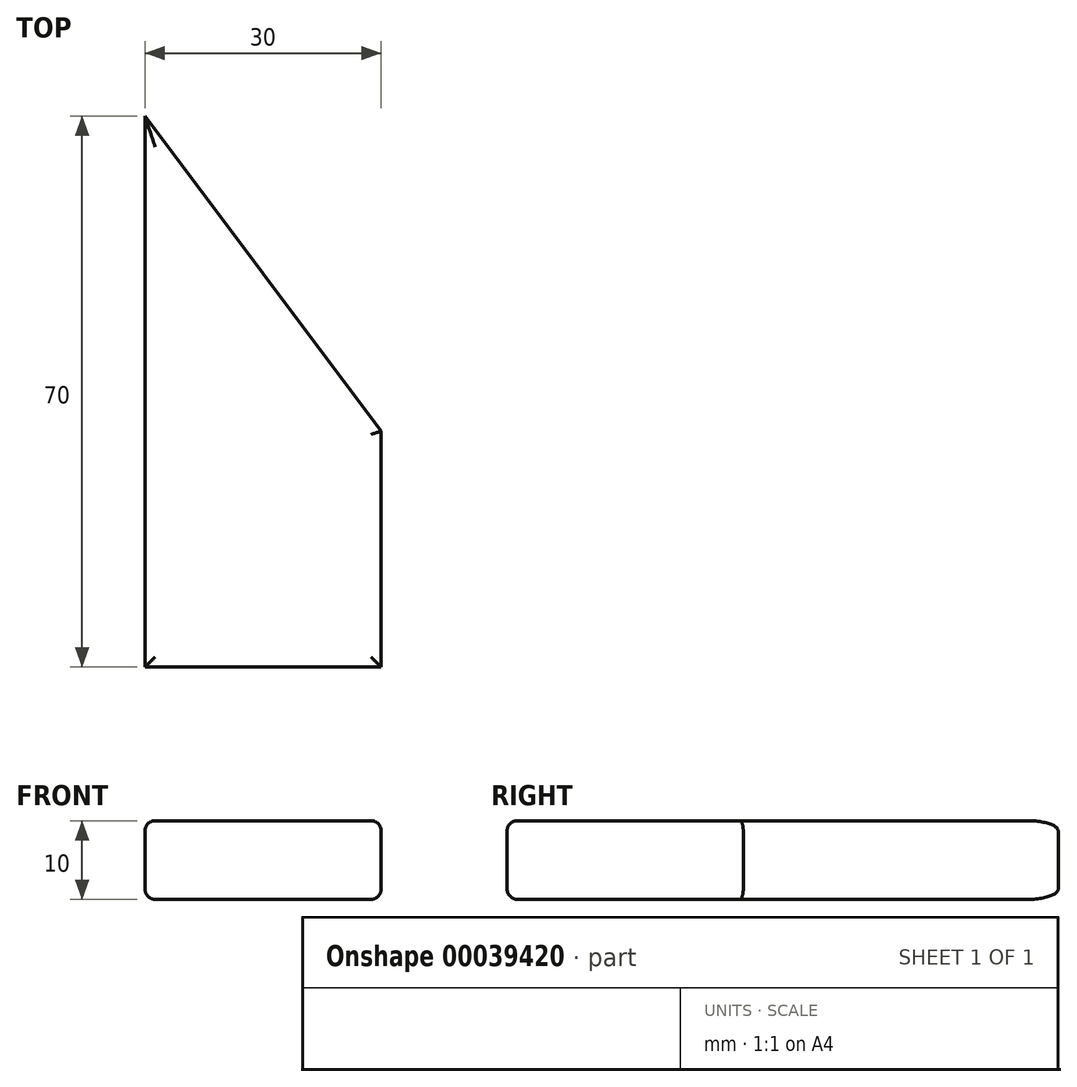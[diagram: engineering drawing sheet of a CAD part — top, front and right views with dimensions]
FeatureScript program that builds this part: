
annotation { "Feature Type Name" : "Feature", "Feature Type Description" : "" }
export const myFeature = defineFeature(function(context is Context, id is Id, definition is map)
    precondition{}
    {
        {
            var Q0;
            Q0=qCreatedBy(makeId("Top.planeOp"),FACE);
            var sketch = newSketch(context, id + "F0", { "sketchPlane" : qUnion([Q0])});
            skLineSegment(sketch, "E0.bottom", {"start": v(-37.15, -6.24) * mm, "end": v(-7.15, -6.24) * mm});
            skLineSegment(sketch, "E0.top", {"start": v(-37.15, -36.24) * mm, "end": v(-7.15, -36.24) * mm});
            skLineSegment(sketch, "E0.left", {"start": v(-37.15, -6.24) * mm, "end": v(-37.15, -36.24) * mm});
            skLineSegment(sketch, "E0.right", {"start": v(-7.15, -6.24) * mm, "end": v(-7.15, -36.24) * mm});
            skLineSegment(sketch, "E1", {"start": v(-37.15, -6.24) * mm, "end": v(-37.15, 33.76) * mm});
            skLineSegment(sketch, "E2", {"start": v(-7.15, -6.24) * mm, "end": v(-37.15, 33.76) * mm});
            skSolve(sketch);
        }
        {
            var Q0;
            Q0=makeQuery(id+"F0.imprint","IMPRINT",FACE,{"disambiguationData":[TD([[makeQuery(id+"F0.imprint","IMPRINT",EDGE,{"derivedFrom":sQuery(id+"F0.wireOp",EDGE,"E0.bottom")}),1.0]])]});
            var Q1;
            Q1=makeQuery(id+"F0.imprint","IMPRINT",FACE,{"disambiguationData":[TD([[makeQuery(id+"F0.imprint","IMPRINT",EDGE,{"derivedFrom":sQuery(id+"F0.wireOp",EDGE,"E0.bottom")}),-1.0]])]});
            extrude(context, id + "F1", {"entities" : qUnion([Q0, Q1]), "depth" : 10 * mm});
        }
        {
            var Q0;
            Q0=makeQuery(id+"F1.opExtrude","CAP_EDGE",EDGE,{"disambiguationData":[OSD([sQuery(id+"F0.wireOp",EDGE,"E0.left"),sQuery(id+"F0.wireOp",EDGE,"E1")])],"isStart":false});
            var Q1;
            Q1=makeQuery(id+"F1.opExtrude","CAP_EDGE",EDGE,{"disambiguationData":[OSD([sQuery(id+"F0.wireOp",EDGE,"E2")])],"isStart":false});
            var Q2;
            Q2=makeQuery(id+"F1.opExtrude","CAP_EDGE",EDGE,{"disambiguationData":[OSD([sQuery(id+"F0.wireOp",EDGE,"E0.right")])],"isStart":false});
            var Q3;
            Q3=makeQuery(id+"F1.opExtrude","CAP_FACE",FACE,{"disambiguationData":[OSD([sQuery(id+"F0.wireOp",EDGE,"E0.top"),sQuery(id+"F0.wireOp",EDGE,"E0.left"),sQuery(id+"F0.wireOp",EDGE,"E0.right"),sQuery(id+"F0.wireOp",EDGE,"E1"),sQuery(id+"F0.wireOp",EDGE,"E2")])],"isStart":false});
            var Q4;
            Q4=makeQuery(id+"F1.opExtrude","CAP_EDGE",EDGE,{"disambiguationData":[OSD([sQuery(id+"F0.wireOp",EDGE,"E0.left"),sQuery(id+"F0.wireOp",EDGE,"E1")])],"isStart":true});
            var Q5;
            Q5=makeQuery(id+"F1.opExtrude","CAP_EDGE",EDGE,{"disambiguationData":[OSD([sQuery(id+"F0.wireOp",EDGE,"E2")])],"isStart":true});
            var Q6;
            Q6=makeQuery(id+"F1.opExtrude","CAP_EDGE",EDGE,{"disambiguationData":[OSD([sQuery(id+"F0.wireOp",EDGE,"E0.right")])],"isStart":true});
            var Q7;
            Q7=makeQuery(id+"F1.opExtrude","CAP_EDGE",EDGE,{"disambiguationData":[OSD([sQuery(id+"F0.wireOp",EDGE,"E0.top")])],"isStart":true});
            fillet(context, id + "F2", {"entities" : qUnion([Q0, Q1, Q2, Q3, Q4, Q5, Q6, Q7]), "radius" : 1.3 * mm, "tangentPropagation" : true, "allowEdgeOverflow" : false});
        }
    });
